# Revit family: Tables-Meeting-Teknion-BAWMG_Wall_Mounted_Glass_Markerboard-R2018
name_source: partatom
category: Furniture
revit_build: Autodesk Revit 2018 (Build: 20170223_1515(x64)
units: mm (PartAtom-declared; Revit-internal decimal feet)

## family parameters
Always vertical = Yes
Cut with Voids When Loaded = No
OmniClass Number = 23.40.20.00
OmniClass Title = General Furniture and Specialties
Room Calculation Point = No
Shared = Yes
Work Plane-Based = No

## types (8) — shared parameters
Assembly Code = E2020200
Manufacturer = Teknion
Manufacturer Fax = 416.661.4586
Part Number = BAWMG
Product Documentation Link = https://www.teknion.com
Product Line = Expansion Casegoods
Product Page URL = https://www.teknion.com
Series = Expansion Casegoods
Sustainability Data = https://www.teknion.com
URL = www.teknion.com
Unit Weight URL = http://www.teknion.com
Warranty = http://www.teknion.com

## per-type parameters (varying)
| type | Description | Height | Model | Pencil Tray Option |
| Non-Magnetic Glass Markerboard Style, 48" h, with Pencil Tray | Wall-Mounted Glass Markerboard, Non-Magnetic Glass Markerboard Style, 48" Height, with Pencil Tray | 48 " | BAWMGG48__Y | Yes |
| Non-Magnetic Glass Markerboard Style, 48" h | Wall-Mounted Glass Markerboard, Non-Magnetic Glass Markerboard Style, 48" Height | 48 " | BAWMGG48__N | No |
| Non-Magnetic Glass Markerboard Style, 52" h | Wall-Mounted Glass Markerboard, Non-Magnetic Glass Markerboard Style, 52" Height | 52 " | BAWMGG52__N | No |
| Non-Magnetic Glass Markerboard Style, 52" h, with Pencil Tray | Wall-Mounted Glass Markerboard, Non-Magnetic Glass Markerboard Style, 52" Height, with Pencil Tray | 52 " | BAWMGG52__Y | Yes |
| Magnetic Glass Markerboard Style, 48" h | Wall-Mounted Glass Markerboard, Magnetic Glass Markerboard Style, 48" Height | 48 " | BAWMGM48__N | No |
| Magnetic Glass Markerboard Style, 48" h, with Pencil Tray | Wall-Mounted Glass Markerboard, Magnetic Glass Markerboard Style, 48" Height, with Pencil Tray | 48 " | BAWMGM48__Y | Yes |
| Magnetic Glass Markerboard Style, 52" h | Wall-Mounted Glass Markerboard, Magnetic Glass Markerboard Style, 52" Height | 52 " | BAWMGM52__N | No |
| Magnetic Glass Markerboard Style, 52" h, with Pencil Tray | Wall-Mounted Glass Markerboard, Magnetic Glass Markerboard Style, 52" Height, with Pencil Tray | 52 " | BAWMGM52__Y | Yes |

## geometry (parser evidence)
native form markers: Sweep x2
no freeform markers — native parametric forms only
